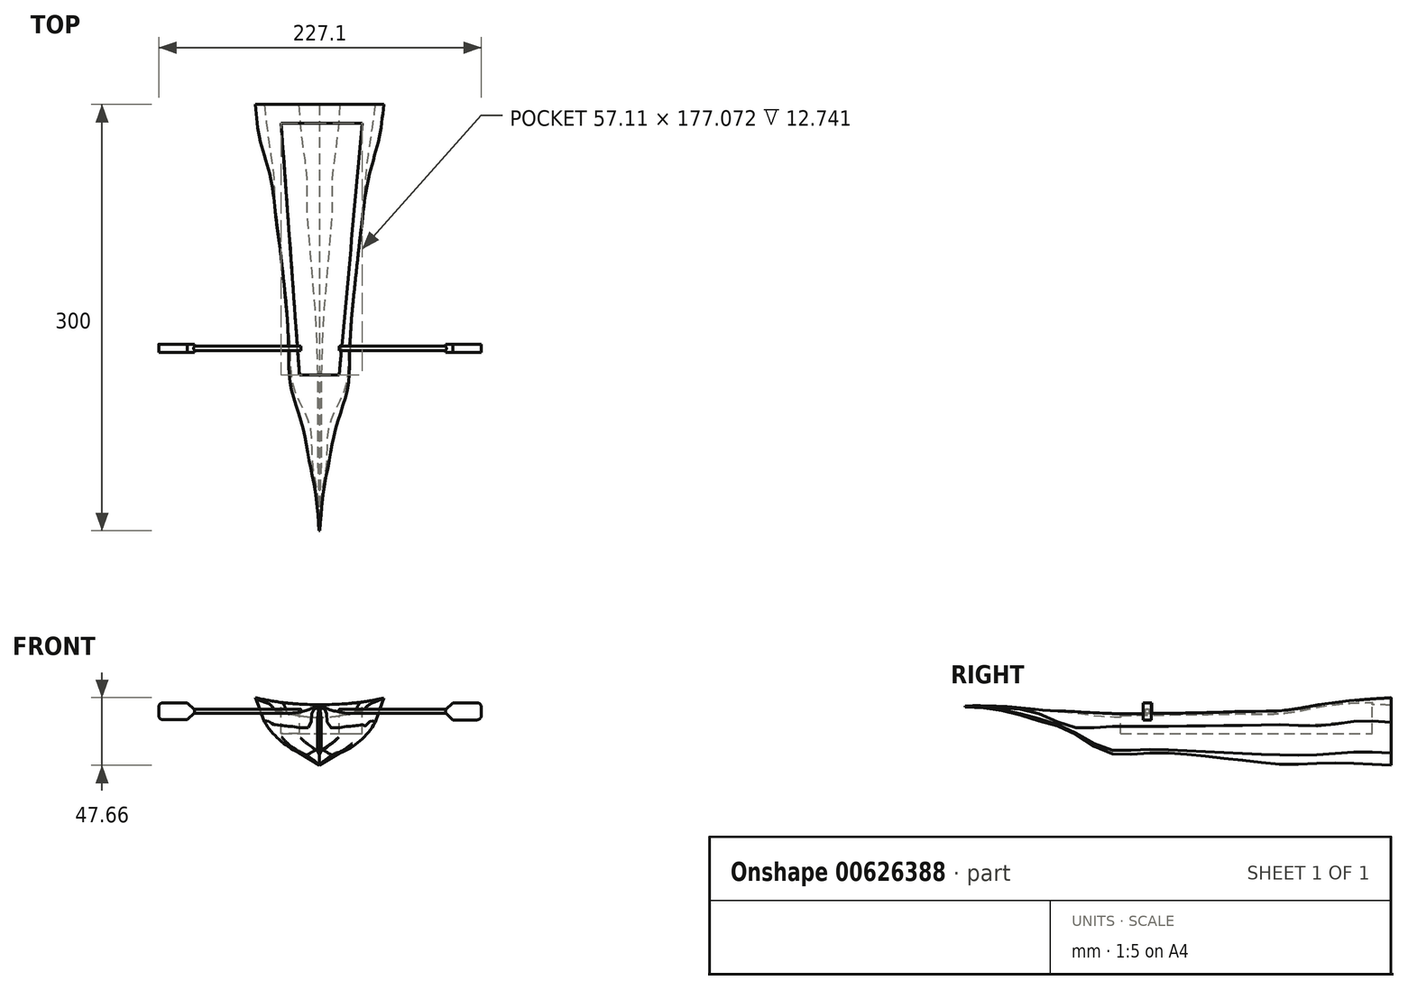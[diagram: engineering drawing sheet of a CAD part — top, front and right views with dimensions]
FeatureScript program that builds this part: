
annotation { "Feature Type Name" : "Feature", "Feature Type Description" : "" }
export const myFeature = defineFeature(function(context is Context, id is Id, definition is map)
    precondition{}
    {
        {
            var Q0;
            Q0=qCreatedBy(makeId("Front.planeOp"),FACE);
            var sketch = newSketch(context, id + "F0", { "sketchPlane" : qUnion([Q0])});
            skLineSegment(sketch, "E0", {"start": v(0, 0) * mm, "end": v(-7, 5) * mm});
            skLineSegment(sketch, "E1", {"start": v(7, 5) * mm, "end": v(0, 0) * mm});
            skArc(sketch, "E2", {"start": v(-27.91, 34.76) * mm, "mid": v(0, 30.75) * mm, "end": v(27.91, 34.76) * mm});
            skArc(sketch, "E3", {"start": v(-27.91, 25) * mm, "mid": v(-19.33, 13.04) * mm, "end": v(-7, 5) * mm});
            skArc(sketch, "E4", {"start": v(7, 5) * mm, "mid": v(19.33, 13.04) * mm, "end": v(27.91, 25) * mm});
            skPoint(sketch, "E5.start.orphan", {"position": v(7, 25) * mm});
            skPoint(sketch, "E6.end.orphan", {"position": v(27.91, 5) * mm});
            skPoint(sketch, "E7.end.orphan", {"position": v(-7, 25) * mm});
            skLineSegment(sketch, "E8", {"start": v(27.91, 25) * mm, "end": v(27.91, 34.76) * mm});
            skLineSegment(sketch, "E9", {"start": v(-27.91, 25) * mm, "end": v(-27.91, 34.76) * mm});
            skPoint(sketch, "E10.orphan", {"position": v(-27.91, 35) * mm});
            skPoint(sketch, "E11.orphan", {"position": v(27.91, 35) * mm});
            skSolve(sketch);
        }
        {
            var Q0;
            Q0=makeQuery(id+"F0.imprint","IMPRINT",FACE,{"disambiguationData":[TD([[makeQuery(id+"F0.imprint","IMPRINT",EDGE,{"derivedFrom":sQuery(id+"F0.wireOp",EDGE,"E0")}),-1.0]])]});
            cPlane(context, id + "F1", {"entities" : qUnion([Q0]), "cplaneType" : CPlaneType.OFFSET, "offset" : 25 * mm, "width" : 150 * mm, "height" : 150 * mm});
        }
        {
            var Q0;
            Q0=qCreatedBy(id+"F1.planeOp",FACE);
            var sketch = newSketch(context, id + "F2", { "sketchPlane" : qUnion([Q0])});
            skLineSegment(sketch, "E12", {"start": v(0, 0) * mm, "end": v(0, 2.5) * mm});
            skLineSegment(sketch, "E13", {"start": v(0, 2.5) * mm, "end": v(4.92, 6.19) * mm});
            skArc(sketch, "E14", {"start": v(4.92, 6.19) * mm, "mid": v(16.37, 14.01) * mm, "end": v(25.2, 24.7) * mm});
            skLineSegment(sketch, "E15", {"start": v(0, 2.5) * mm, "end": v(0, 5.33) * mm});
            skLineSegment(sketch, "E16", {"start": v(0, 2.5) * mm, "end": v(-4.92, 6.19) * mm});
            skArc(sketch, "E17", {"start": v(-25.01, 24.7) * mm, "mid": v(-16.4, 13.89) * mm, "end": v(-4.92, 6.19) * mm});
            skPoint(sketch, "E18.end.orphan", {"position": v(-25.01, 31.8) * mm});
            skLineSegment(sketch, "E19", {"start": v(-25.01, 24.7) * mm, "end": v(-25.01, 34.04) * mm});
            skPoint(sketch, "E20.end.orphan", {"position": v(25.2, 31.8) * mm});
            skLineSegment(sketch, "E21", {"start": v(25.2, 24.7) * mm, "end": v(25.2, 34.03) * mm});
            skArc(sketch, "E22", {"start": v(-25.01, 34.04) * mm, "mid": v(0.1, 30.82) * mm, "end": v(25.2, 34.03) * mm});
            skSolve(sketch);
        }
        {
            var Q0;
            Q0=makeQuery(id+"F2.imprint","IMPRINT",FACE,{"disambiguationData":[TD([[makeQuery(id+"F2.imprint","IMPRINT",EDGE,{"derivedFrom":sQuery(id+"F2.wireOp",EDGE,"E13")}),1.0]])]});
            cPlane(context, id + "F3", {"entities" : qUnion([Q0]), "cplaneType" : CPlaneType.OFFSET, "offset" : 25 * mm, "width" : 150 * mm, "height" : 150 * mm});
        }
        {
            var Q0;
            Q0=qCreatedBy(id+"F3.planeOp",FACE);
            var sketch = newSketch(context, id + "F4", { "sketchPlane" : qUnion([Q0])});
            skLineSegment(sketch, "E23", {"start": v(0, 5.17) * mm, "end": v(2.84, 7.4) * mm});
            skLineSegment(sketch, "E24", {"start": v(0, 5.17) * mm, "end": v(-2.84, 7.4) * mm});
            skArc(sketch, "E25", {"start": v(2.84, 7.4) * mm, "mid": v(14, 14.51) * mm, "end": v(22.71, 24.47) * mm});
            skArc(sketch, "E26", {"start": v(-22.66, 24.44) * mm, "mid": v(-13.98, 14.49) * mm, "end": v(-2.84, 7.4) * mm});
            skLineSegment(sketch, "E27", {"start": v(-22.66, 24.44) * mm, "end": v(-22.66, 33.5) * mm});
            skLineSegment(sketch, "E28", {"start": v(22.71, 24.47) * mm, "end": v(22.71, 33.46) * mm});
            skArc(sketch, "E29", {"start": v(-22.66, 33.5) * mm, "mid": v(0.03, 30.83) * mm, "end": v(22.71, 33.46) * mm});
            skSolve(sketch);
        }
        {
            var Q0;
            Q0=qCreatedBy(id+"F3.planeOp",FACE);
            cPlane(context, id + "F5", {"entities" : qUnion([Q0]), "cplaneType" : CPlaneType.OFFSET, "offset" : 25 * mm, "width" : 150 * mm, "height" : 150 * mm});
        }
        {
            var Q0;
            Q0=qCreatedBy(makeId("Front.planeOp"),FACE);
            cPlane(context, id + "F6", {"entities" : qUnion([Q0]), "cplaneType" : CPlaneType.OFFSET, "offset" : 25 * mm, "oppositeDirection" : true, "width" : 150 * mm, "height" : 150 * mm});
        }
        {
            var Q0;
            Q0=qCreatedBy(id+"F6.planeOp",FACE);
            var sketch = newSketch(context, id + "F7", { "sketchPlane" : qUnion([Q0])});
            skLineSegment(sketch, "E30", {"start": v(-8.83, 3.96) * mm, "end": v(0, -2.66) * mm});
            skLineSegment(sketch, "E31", {"start": v(8.85, 3.96) * mm, "end": v(0, -2.66) * mm});
            skArc(sketch, "E32", {"start": v(-31.1, 25.34) * mm, "mid": v(-22.18, 12.34) * mm, "end": v(-8.83, 3.96) * mm});
            skArc(sketch, "E33", {"start": v(8.85, 3.96) * mm, "mid": v(22.33, 12.1) * mm, "end": v(30.9, 25.3) * mm});
            skLineSegment(sketch, "E34", {"start": v(30.9, 25.3) * mm, "end": v(30.9, 35.5) * mm});
            skLineSegment(sketch, "E35", {"start": v(-31.1, 25.34) * mm, "end": v(-31.1, 35.5) * mm});
            skArc(sketch, "E36", {"start": v(-31.1, 35.5) * mm, "mid": v(-0.1, 30.84) * mm, "end": v(30.9, 35.5) * mm});
            skSolve(sketch);
        }
        {
            var Q0;
            Q0=qCreatedBy(id+"F5.planeOp",FACE);
            var sketch = newSketch(context, id + "F8", { "sketchPlane" : qUnion([Q0])});
            skLineSegment(sketch, "E37", {"start": v(0, 0) * mm, "end": v(0, 5.2) * mm});
            skLineSegment(sketch, "E38", {"start": v(0, 5.2) * mm, "end": v(1.7, 7.89) * mm});
            skLineSegment(sketch, "E39", {"start": v(0, 5.2) * mm, "end": v(0, 15.24) * mm});
            skLineSegment(sketch, "E40", {"start": v(0, 5.2) * mm, "end": v(-1.7, 7.89) * mm});
            skArc(sketch, "E41", {"start": v(-20.62, 24.18) * mm, "mid": v(-12.06, 14.98) * mm, "end": v(-1.7, 7.89) * mm});
            skArc(sketch, "E42", {"start": v(1.7, 7.89) * mm, "mid": v(11.95, 14.95) * mm, "end": v(20.33, 24.16) * mm});
            skLineSegment(sketch, "E43", {"start": v(20.33, 24.16) * mm, "end": v(21.38, 33.19) * mm});
            skLineSegment(sketch, "E44", {"start": v(-20.62, 24.18) * mm, "end": v(-21.68, 33.2) * mm});
            skArc(sketch, "E45", {"start": v(-21.68, 33.2) * mm, "mid": v(-0.15, 30.86) * mm, "end": v(21.38, 33.19) * mm});
            skSolve(sketch);
        }
        {
            var Q0;
            Q0=qCreatedBy(id+"F5.planeOp",FACE);
            cPlane(context, id + "F9", {"entities" : qUnion([Q0]), "cplaneType" : CPlaneType.OFFSET, "offset" : 25 * mm, "width" : 150 * mm, "height" : 150 * mm});
        }
        {
            var Q0;
            Q0=qCreatedBy(id+"F6.planeOp",FACE);
            cPlane(context, id + "F10", {"entities" : qUnion([Q0]), "cplaneType" : CPlaneType.OFFSET, "offset" : 25 * mm, "oppositeDirection" : true, "width" : 150 * mm, "height" : 150 * mm});
        }
        {
            var Q0;
            Q0=qCreatedBy(id+"F10.planeOp",FACE);
            var sketch = newSketch(context, id + "F11", { "sketchPlane" : qUnion([Q0])});
            skLineSegment(sketch, "E46", {"start": v(0, -1.8) * mm, "end": v(-9.14, 4.4) * mm});
            skLineSegment(sketch, "E47", {"start": v(0, -1.8) * mm, "end": v(9.14, 4.4) * mm});
            skArc(sketch, "E48", {"start": v(9.14, 4.4) * mm, "mid": v(22.92, 12.09) * mm, "end": v(32.5, 24.6) * mm});
            skArc(sketch, "E49", {"start": v(-32.38, 25.49) * mm, "mid": v(-22.75, 12.75) * mm, "end": v(-9.14, 4.4) * mm});
            skLineSegment(sketch, "E50", {"start": v(-32.38, 25.49) * mm, "end": v(-34.73, 39.5) * mm});
            skLineSegment(sketch, "E51", {"start": v(32.5, 24.6) * mm, "end": v(35.04, 39.5) * mm});
            skArc(sketch, "E52", {"start": v(-34.73, 39.5) * mm, "mid": v(0.15, 36.4) * mm, "end": v(35.04, 39.5) * mm});
            skSolve(sketch);
        }
        {
            var Q0;
            Q0=qCreatedBy(id+"F10.planeOp",FACE);
            cPlane(context, id + "F12", {"entities" : qUnion([Q0]), "cplaneType" : CPlaneType.OFFSET, "offset" : 25 * mm, "oppositeDirection" : true, "width" : 150 * mm, "height" : 150 * mm});
        }
        {
            var Q0;
            Q0=qCreatedBy(id+"F12.planeOp",FACE);
            var sketch = newSketch(context, id + "F13", { "sketchPlane" : qUnion([Q0])});
            skLineSegment(sketch, "E53", {"start": v(0, -1.91) * mm, "end": v(-12.35, 6.1) * mm});
            skLineSegment(sketch, "E54", {"start": v(0, -1.91) * mm, "end": v(12.35, 6.1) * mm});
            skArc(sketch, "E55", {"start": v(-35.84, 27.87) * mm, "mid": v(-25.75, 15.2) * mm, "end": v(-12.35, 6.1) * mm});
            skLineSegment(sketch, "E56", {"start": v(-35.84, 27.87) * mm, "end": v(-41.84, 42.55) * mm});
            skLineSegment(sketch, "E57", {"start": v(35.75, 27.87) * mm, "end": v(41.75, 42.55) * mm});
            skArc(sketch, "E58", {"start": v(-41.84, 42.55) * mm, "mid": v(-0.05, 39.36) * mm, "end": v(41.75, 42.55) * mm});
            skArc(sketch, "E59", {"start": v(12.35, 6.1) * mm, "mid": v(26.45, 14.4) * mm, "end": v(35.75, 27.87) * mm});
            skSolve(sketch);
        }
        {
            var Q0;
            Q0=qCreatedBy(id+"F12.planeOp",FACE);
            cPlane(context, id + "F14", {"entities" : qUnion([Q0]), "cplaneType" : CPlaneType.OFFSET, "offset" : 25 * mm, "oppositeDirection" : true, "width" : 150 * mm, "height" : 150 * mm});
        }
        {
            var Q0;
            Q0=qCreatedBy(id+"F14.planeOp",FACE);
            var sketch = newSketch(context, id + "F15", { "sketchPlane" : qUnion([Q0])});
            skLineSegment(sketch, "E60", {"start": v(0, -3.25) * mm, "end": v(-14.6, 5.86) * mm});
            skLineSegment(sketch, "E61", {"start": v(0, -3.25) * mm, "end": v(0, -1.07) * mm});
            skArc(sketch, "E62", {"start": v(-38.72, 27.45) * mm, "mid": v(-28.26, 14.88) * mm, "end": v(-14.6, 5.86) * mm});
            skPoint(sketch, "E63.end.orphan", {"position": v(14.6, 5.86) * mm});
            skLineSegment(sketch, "E64", {"start": v(0, -3.25) * mm, "end": v(14.32, 5.33) * mm});
            skArc(sketch, "E65", {"start": v(14.32, 5.33) * mm, "mid": v(28.68, 14.05) * mm, "end": v(39.32, 27.05) * mm});
            skLineSegment(sketch, "E66", {"start": v(39.32, 27.05) * mm, "end": v(45.35, 44.15) * mm});
            skLineSegment(sketch, "E67", {"start": v(-38.72, 27.45) * mm, "end": v(-44.96, 44.4) * mm});
            skArc(sketch, "E68", {"start": v(-44.96, 44.4) * mm, "mid": v(0.18, 39.17) * mm, "end": v(45.35, 44.15) * mm});
            skSolve(sketch);
        }
        {
            var Q0;
            Q0=qCreatedBy(id+"F9.planeOp",FACE);
            var sketch = newSketch(context, id + "F16", { "sketchPlane" : qUnion([Q0])});
            skLineSegment(sketch, "E69", {"start": v(0, 6) * mm, "end": v(1.23, 8.16) * mm});
            skLineSegment(sketch, "E70", {"start": v(0, 6) * mm, "end": v(-1.24, 8.16) * mm});
            skArc(sketch, "E71", {"start": v(1.23, 8.16) * mm, "mid": v(10.4, 15.25) * mm, "end": v(17.92, 24.05) * mm});
            skArc(sketch, "E72", {"start": v(-18.07, 23.97) * mm, "mid": v(-10.38, 15.3) * mm, "end": v(-1.24, 8.16) * mm});
            skLineSegment(sketch, "E73", {"start": v(-18.07, 23.97) * mm, "end": v(-19.75, 33.38) * mm});
            skLineSegment(sketch, "E74", {"start": v(17.92, 24.05) * mm, "end": v(19.83, 33.3) * mm});
            skArc(sketch, "E75", {"start": v(-19.75, 33.38) * mm, "mid": v(0.03, 30.84) * mm, "end": v(19.83, 33.3) * mm});
            skSolve(sketch);
        }
        {
            var Q0;
            Q0=qCreatedBy(id+"F9.planeOp",FACE);
            cPlane(context, id + "F17", {"entities" : qUnion([Q0]), "cplaneType" : CPlaneType.OFFSET, "offset" : 25 * mm, "width" : 150 * mm, "height" : 150 * mm});
        }
        {
            var Q0;
            Q0=qCreatedBy(id+"F17.planeOp",FACE);
            var sketch = newSketch(context, id + "F18", { "sketchPlane" : qUnion([Q0])});
            skPoint(sketch, "E76.top.end.orphan", {"position": v(-12.21, 6.12) * mm});
            skPoint(sketch, "E76.left.end.orphan", {"position": v(12.21, 6.12) * mm});
            skPoint(sketch, "E77", {"position": v(0, 36.5) * mm});
            skPoint(sketch, "E78", {"position": v(-12.36, 34.65) * mm});
            skArc(sketch, "E79", {"start": v(-12.36, 34.65) * mm, "mid": v(0, 33.63) * mm, "end": v(12.36, 34.65) * mm});
            skPoint(sketch, "E80.top.start.orphan", {"position": v(-12.36, 38.34) * mm});
            skPoint(sketch, "E80.right.end.orphan", {"position": v(12.36, 38.34) * mm});
            skPoint(sketch, "E81.middle", {"position": v(0, 26.55) * mm});
            skArc(sketch, "E82", {"start": v(7.07, 23.72) * mm, "mid": v(10.26, 28.92) * mm, "end": v(12.36, 34.65) * mm});
            skArc(sketch, "E83", {"start": v(-12.36, 34.65) * mm, "mid": v(-10.3, 28.9) * mm, "end": v(-7.07, 23.72) * mm});
            skPoint(sketch, "E83.endSnap0", {"position": v(-7.07, 26.55) * mm});
            skPoint(sketch, "E84.orphan", {"position": v(-7.07, 33.96) * mm});
            skPoint(sketch, "E85.orphan", {"position": v(7.07, 33.96) * mm});
            skPoint(sketch, "E81.top.end.orphan", {"position": v(-7.07, 19.14) * mm});
            skPoint(sketch, "E81.top.start.orphan", {"position": v(7.07, 19.14) * mm});
            skPoint(sketch, "E86.start.orphan", {"position": v(0, 20.2) * mm});
            skLineSegment(sketch, "E87", {"start": v(-7.07, 23.72) * mm, "end": v(-1.16, 21.26) * mm});
            skLineSegment(sketch, "E88", {"start": v(-1.16, 21.26) * mm, "end": v(0, 20.2) * mm});
            skLineSegment(sketch, "E89", {"start": v(0, 20.2) * mm, "end": v(1.16, 21.26) * mm});
            skLineSegment(sketch, "E90", {"start": v(7.07, 23.72) * mm, "end": v(1.16, 21.26) * mm});
            skPoint(sketch, "E91.top.end.orphan", {"position": v(1.16, 19.13) * mm});
            skPoint(sketch, "E91.left.end.orphan", {"position": v(-1.16, 19.13) * mm});
            skSolve(sketch);
        }
        {
            var Q0;
            Q0=qCreatedBy(id+"F17.planeOp",FACE);
            cPlane(context, id + "F19", {"entities" : qUnion([Q0]), "cplaneType" : CPlaneType.OFFSET, "offset" : 25 * mm, "width" : 150 * mm, "height" : 150 * mm});
        }
        {
            var Q0;
            Q0=qCreatedBy(id+"F19.planeOp",FACE);
            var sketch = newSketch(context, id + "F20", { "sketchPlane" : qUnion([Q0])});
            skPoint(sketch, "E92", {"position": v(0, 28.74) * mm});
            skLineSegment(sketch, "E93", {"start": v(0, 28.74) * mm, "end": v(1.2, 30.13) * mm});
            skLineSegment(sketch, "E94", {"start": v(0, 28.74) * mm, "end": v(-1.2, 30.13) * mm});
            skPoint(sketch, "E95.top.start.orphan", {"position": v(1.2, 27.36) * mm});
            skPoint(sketch, "E95.right.end.orphan", {"position": v(-1.2, 27.36) * mm});
            skPoint(sketch, "E96.top.end.orphan", {"position": v(-4.76, 21.83) * mm});
            skPoint(sketch, "E96.top.start.orphan", {"position": v(4.76, 21.83) * mm});
            skPoint(sketch, "E97.top.end.orphan", {"position": v(-12.6, 14.32) * mm});
            skPoint(sketch, "E97.top.start.orphan", {"position": v(12.6, 14.32) * mm});
            skPoint(sketch, "E98.start.orphan", {"position": v(-12.6, 43.17) * mm});
            skPoint(sketch, "E99.end.orphan", {"position": v(12.6, 43.17) * mm});
            skPoint(sketch, "E100.end.orphan", {"position": v(4.76, 35.66) * mm});
            skPoint(sketch, "E101.end.orphan", {"position": v(-4.76, 35.66) * mm});
            skPoint(sketch, "E102.top.end.orphan", {"position": v(-4.37, 23.59) * mm});
            skPoint(sketch, "E102.top.start.orphan", {"position": v(4.37, 23.59) * mm});
            skLineSegment(sketch, "E103", {"start": v(1.2, 30.13) * mm, "end": v(5.1, 33.9) * mm});
            skLineSegment(sketch, "E104", {"start": v(-1.2, 30.13) * mm, "end": v(-5.36, 33.9) * mm});
            skPoint(sketch, "E105.orphan", {"position": v(-4.37, 33.9) * mm});
            skPoint(sketch, "E106.end.orphan", {"position": v(4.37, 33.9) * mm});
            skPoint(sketch, "E107.top.end.orphan", {"position": v(-6.68, 20.51) * mm});
            skPoint(sketch, "E107.top.start.orphan", {"position": v(6.68, 20.51) * mm});
            skPoint(sketch, "E107.bottom.end.orphan", {"position": v(-6.68, 36.97) * mm});
            skPoint(sketch, "E107.bottom.start.orphan", {"position": v(6.68, 36.97) * mm});
            skArc(sketch, "E108", {"start": v(5.1, 33.9) * mm, "mid": v(6.22, 34.84) * mm, "end": v(7.01, 36.08) * mm});
            skArc(sketch, "E109", {"start": v(-7.23, 36.08) * mm, "mid": v(-6.47, 34.84) * mm, "end": v(-5.36, 33.9) * mm});
            skArc(sketch, "E110", {"start": v(-7.23, 36.08) * mm, "mid": v(-0.1, 35.56) * mm, "end": v(7.01, 36.08) * mm});
            skSolve(sketch);
        }
        {
            var Q0;
            Q0=qCreatedBy(id+"F19.planeOp",FACE);
            cPlane(context, id + "F21", {"entities" : qUnion([Q0]), "cplaneType" : CPlaneType.OFFSET, "offset" : 25 * mm, "width" : 150 * mm, "height" : 150 * mm});
        }
        {
            var Q0;
            Q0=qCreatedBy(id+"F21.planeOp",FACE);
            var sketch = newSketch(context, id + "F22", { "sketchPlane" : qUnion([Q0])});
            skPoint(sketch, "E111", {"position": v(0, 35.66) * mm});
            skLineSegment(sketch, "E112", {"start": v(0, 35.66) * mm, "end": v(0.41, 36.23) * mm});
            skLineSegment(sketch, "E113", {"start": v(1.33, 37.34) * mm, "end": v(0.41, 36.23) * mm});
            skLineSegment(sketch, "E114", {"start": v(-0.41, 36.23) * mm, "end": v(-1.33, 37.34) * mm});
            skLineSegment(sketch, "E115", {"start": v(0, 35.66) * mm, "end": v(-0.41, 36.23) * mm});
            skArc(sketch, "E116", {"start": v(1.33, 37.34) * mm, "mid": v(1.96, 37.77) * mm, "end": v(2.52, 38.3) * mm});
            skArc(sketch, "E117", {"start": v(-2.52, 38.3) * mm, "mid": v(-1.96, 37.78) * mm, "end": v(-1.33, 37.34) * mm});
            skPoint(sketch, "E118.top.end.orphan", {"position": v(-1.33, 33.99) * mm});
            skPoint(sketch, "E118.top.start.orphan", {"position": v(1.33, 33.99) * mm});
            skPoint(sketch, "E119.top.end.orphan", {"position": v(-2.52, 33.02) * mm});
            skPoint(sketch, "E119.left.end.orphan", {"position": v(2.52, 33.02) * mm});
            skPoint(sketch, "E120.top.start.orphan", {"position": v(0.41, 35.1) * mm});
            skPoint(sketch, "E120.right.end.orphan", {"position": v(-0.41, 35.1) * mm});
            skArc(sketch, "E121", {"start": v(-2.52, 38.3) * mm, "mid": v(0, 38.12) * mm, "end": v(2.52, 38.3) * mm});
            skSolve(sketch);
        }
        {
            var Q0;
            Q0=qCreatedBy(id+"F21.planeOp",FACE);
            cPlane(context, id + "F23", {"entities" : qUnion([Q0]), "cplaneType" : CPlaneType.OFFSET, "offset" : 25 * mm, "width" : 150 * mm, "height" : 150 * mm});
        }
        {
            var Q0;
            Q0=qCreatedBy(id+"F23.planeOp",FACE);
            var sketch = newSketch(context, id + "F24", { "sketchPlane" : qUnion([Q0])});
            skArc(sketch, "E122", {"start": v(-0.4, 38.6) * mm, "mid": v(0, 38.53) * mm, "end": v(0.4, 38.6) * mm});
            skArc(sketch, "E123", {"start": v(0.25, 38.29) * mm, "mid": v(0.35, 38.43) * mm, "end": v(0.4, 38.6) * mm});
            skArc(sketch, "E124", {"start": v(-0.4, 38.6) * mm, "mid": v(-0.35, 38.43) * mm, "end": v(-0.25, 38.29) * mm});
            skLineSegment(sketch, "E125", {"start": v(0.05, 38.08) * mm, "end": v(0.25, 38.29) * mm});
            skLineSegment(sketch, "E126", {"start": v(-0.05, 38.08) * mm, "end": v(-0.25, 38.29) * mm});
            skLineSegment(sketch, "E127", {"start": v(-0.05, 38.08) * mm, "end": v(0, 38) * mm});
            skLineSegment(sketch, "E128", {"start": v(0, 38) * mm, "end": v(0.05, 38.08) * mm});
            skSolve(sketch);
        }
        {
            var Q0;
            Q0=makeQuery(id+"F15.imprint","IMPRINT",FACE,{"disambiguationData":[TD([[makeQuery(id+"F15.imprint","IMPRINT",EDGE,{"derivedFrom":sQuery(id+"F15.wireOp",EDGE,"E60")}),-1.0]])]});
            var Q1;
            Q1=makeQuery(id+"F13.imprint","IMPRINT",FACE,{"disambiguationData":[TD([[makeQuery(id+"F13.imprint","IMPRINT",EDGE,{"derivedFrom":sQuery(id+"F13.wireOp",EDGE,"E53")}),-1.0]])]});
            var Q2;
            Q2=makeQuery(id+"F11.imprint","IMPRINT",FACE,{"disambiguationData":[TD([[makeQuery(id+"F11.imprint","IMPRINT",EDGE,{"derivedFrom":sQuery(id+"F11.wireOp",EDGE,"E46")}),-1.0]])]});
            var Q3;
            Q3=makeQuery(id+"F7.imprint","IMPRINT",FACE,{"disambiguationData":[TD([[makeQuery(id+"F7.imprint","IMPRINT",EDGE,{"derivedFrom":sQuery(id+"F7.wireOp",EDGE,"E30")}),1.0]])]});
            var Q4;
            Q4=makeQuery(id+"F0.imprint","IMPRINT",FACE,{"disambiguationData":[TD([[makeQuery(id+"F0.imprint","IMPRINT",EDGE,{"derivedFrom":sQuery(id+"F0.wireOp",EDGE,"E0")}),-1.0]])]});
            var Q5;
            Q5=makeQuery(id+"F2.imprint","IMPRINT",FACE,{"disambiguationData":[TD([[makeQuery(id+"F2.imprint","IMPRINT",EDGE,{"derivedFrom":sQuery(id+"F2.wireOp",EDGE,"E13")}),1.0]])]});
            var Q6;
            Q6=makeQuery(id+"F4.imprint","IMPRINT",FACE,{"disambiguationData":[TD([[makeQuery(id+"F4.imprint","IMPRINT",EDGE,{"derivedFrom":sQuery(id+"F4.wireOp",EDGE,"E23")}),1.0]])]});
            var Q7;
            Q7=makeQuery(id+"F8.imprint","IMPRINT",FACE,{"disambiguationData":[TD([[makeQuery(id+"F8.imprint","IMPRINT",EDGE,{"derivedFrom":sQuery(id+"F8.wireOp",EDGE,"E38")}),1.0]])]});
            var Q8;
            Q8=makeQuery(id+"F16.imprint","IMPRINT",FACE,{"disambiguationData":[TD([[makeQuery(id+"F16.imprint","IMPRINT",EDGE,{"derivedFrom":sQuery(id+"F16.wireOp",EDGE,"E69")}),1.0]])]});
            var Q9;
            Q9=makeQuery(id+"F18.imprint","IMPRINT",FACE,{"disambiguationData":[TD([[makeQuery(id+"F18.imprint","IMPRINT",EDGE,{"derivedFrom":sQuery(id+"F18.wireOp",EDGE,"E79")}),-1.0]])]});
            var Q10;
            Q10=makeQuery(id+"F20.imprint","IMPRINT",FACE,{"disambiguationData":[TD([[makeQuery(id+"F20.imprint","IMPRINT",EDGE,{"derivedFrom":sQuery(id+"F20.wireOp",EDGE,"E93")}),1.0]])]});
            var Q11;
            Q11=makeQuery(id+"F22.imprint","IMPRINT",FACE,{"disambiguationData":[TD([[makeQuery(id+"F22.imprint","IMPRINT",EDGE,{"derivedFrom":sQuery(id+"F22.wireOp",EDGE,"E112")}),1.0]])]});
            var Q12;
            Q12=makeQuery(id+"F24.imprint","IMPRINT",FACE,{"disambiguationData":[TD([[makeQuery(id+"F24.imprint","IMPRINT",EDGE,{"derivedFrom":sQuery(id+"F24.wireOp",EDGE,"E122")}),-1.0]])]});
            var Q13;
            Q13=makeQuery(id+"F15.imprint","IMPRINT",FACE,{"disambiguationData":[TD([[makeQuery(id+"F15.imprint","IMPRINT",EDGE,{"derivedFrom":sQuery(id+"F15.wireOp",EDGE,"E60")}),-1.0]])]});
            var Q14;
            Q14=makeQuery(id+"F13.imprint","IMPRINT",FACE,{"disambiguationData":[TD([[makeQuery(id+"F13.imprint","IMPRINT",EDGE,{"derivedFrom":sQuery(id+"F13.wireOp",EDGE,"E53")}),-1.0]])]});
            var Q15;
            Q15=makeQuery(id+"F11.imprint","IMPRINT",FACE,{"disambiguationData":[TD([[makeQuery(id+"F11.imprint","IMPRINT",EDGE,{"derivedFrom":sQuery(id+"F11.wireOp",EDGE,"E46")}),-1.0]])]});
            var Q16;
            Q16=makeQuery(id+"F7.imprint","IMPRINT",FACE,{"disambiguationData":[TD([[makeQuery(id+"F7.imprint","IMPRINT",EDGE,{"derivedFrom":sQuery(id+"F7.wireOp",EDGE,"E30")}),1.0]])]});
            var Q17;
            Q17=makeQuery(id+"F0.imprint","IMPRINT",FACE,{"disambiguationData":[TD([[makeQuery(id+"F0.imprint","IMPRINT",EDGE,{"derivedFrom":sQuery(id+"F0.wireOp",EDGE,"E0")}),-1.0]])]});
            var Q18;
            Q18=makeQuery(id+"F2.imprint","IMPRINT",FACE,{"disambiguationData":[TD([[makeQuery(id+"F2.imprint","IMPRINT",EDGE,{"derivedFrom":sQuery(id+"F2.wireOp",EDGE,"E13")}),1.0]])]});
            var Q19;
            Q19=makeQuery(id+"F4.imprint","IMPRINT",FACE,{"disambiguationData":[TD([[makeQuery(id+"F4.imprint","IMPRINT",EDGE,{"derivedFrom":sQuery(id+"F4.wireOp",EDGE,"E23")}),1.0]])]});
            var Q20;
            Q20=makeQuery(id+"F8.imprint","IMPRINT",FACE,{"disambiguationData":[TD([[makeQuery(id+"F8.imprint","IMPRINT",EDGE,{"derivedFrom":sQuery(id+"F8.wireOp",EDGE,"E38")}),1.0]])]});
            var Q21;
            Q21=makeQuery(id+"F16.imprint","IMPRINT",FACE,{"disambiguationData":[TD([[makeQuery(id+"F16.imprint","IMPRINT",EDGE,{"derivedFrom":sQuery(id+"F16.wireOp",EDGE,"E69")}),1.0]])]});
            var Q22;
            Q22=makeQuery(id+"F18.imprint","IMPRINT",FACE,{"disambiguationData":[TD([[makeQuery(id+"F18.imprint","IMPRINT",EDGE,{"derivedFrom":sQuery(id+"F18.wireOp",EDGE,"E79")}),-1.0]])]});
            var Q23;
            Q23=makeQuery(id+"F20.imprint","IMPRINT",FACE,{"disambiguationData":[TD([[makeQuery(id+"F20.imprint","IMPRINT",EDGE,{"derivedFrom":sQuery(id+"F20.wireOp",EDGE,"E93")}),1.0]])]});
            var Q24;
            Q24=makeQuery(id+"F22.imprint","IMPRINT",FACE,{"disambiguationData":[TD([[makeQuery(id+"F22.imprint","IMPRINT",EDGE,{"derivedFrom":sQuery(id+"F22.wireOp",EDGE,"E112")}),1.0]])]});
            var Q25;
            Q25=makeQuery(id+"F24.imprint","IMPRINT",FACE,{"disambiguationData":[TD([[makeQuery(id+"F24.imprint","IMPRINT",EDGE,{"derivedFrom":sQuery(id+"F24.wireOp",EDGE,"E122")}),-1.0]])]});
            loft(context, id + "F25", {"sheetProfilesArray" : [{ "sheetProfileEntities" : qUnion([Q0]) }, { "sheetProfileEntities" : qUnion([Q1]) }, { "sheetProfileEntities" : qUnion([Q2]) }, { "sheetProfileEntities" : qUnion([Q3]) }, { "sheetProfileEntities" : qUnion([Q4]) }, { "sheetProfileEntities" : qUnion([Q5]) }, { "sheetProfileEntities" : qUnion([Q6]) }, { "sheetProfileEntities" : qUnion([Q7]) }, { "sheetProfileEntities" : qUnion([Q8]) }, { "sheetProfileEntities" : qUnion([Q9]) }, { "sheetProfileEntities" : qUnion([Q10]) }, { "sheetProfileEntities" : qUnion([Q11]) }, { "sheetProfileEntities" : qUnion([Q12]) }], "wireProfilesArray" : [{ "wireProfileEntities" : qUnion([Q13]) }, { "wireProfileEntities" : qUnion([Q14]) }, { "wireProfileEntities" : qUnion([Q15]) }, { "wireProfileEntities" : qUnion([Q16]) }, { "wireProfileEntities" : qUnion([Q17]) }, { "wireProfileEntities" : qUnion([Q18]) }, { "wireProfileEntities" : qUnion([Q19]) }, { "wireProfileEntities" : qUnion([Q20]) }, { "wireProfileEntities" : qUnion([Q21]) }, { "wireProfileEntities" : qUnion([Q22]) }, { "wireProfileEntities" : qUnion([Q23]) }, { "wireProfileEntities" : qUnion([Q24]) }, { "wireProfileEntities" : qUnion([Q25]) }]});
        }
        {
            var Q0;
            Q0=qCreatedBy(makeId("Top.planeOp"),FACE);
            cPlane(context, id + "F26", {"entities" : qUnion([Q0]), "cplaneType" : CPlaneType.OFFSET, "offset" : 46 * mm, "width" : 150 * mm, "height" : 150 * mm});
        }
        {
            var Q0;
            Q0=qCreatedBy(id+"F26.planeOp",FACE);
            var sketch = newSketch(context, id + "F27", { "sketchPlane" : qUnion([Q0])});
            skLineSegment(sketch, "E129", {"start": v(-14.07, -90.3) * mm, "end": v(13.94, -90.3) * mm});
            skLineSegment(sketch, "E130", {"start": v(13.94, -90.3) * mm, "end": v(30.22, 86.76) * mm});
            skLineSegment(sketch, "E131", {"start": v(-14.07, -90.3) * mm, "end": v(-26.89, 86.76) * mm});
            skLineSegment(sketch, "E132", {"start": v(-26.89, 86.76) * mm, "end": v(30.22, 86.76) * mm});
            skSolve(sketch);
        }
        {
            var Q0;
            Q0=makeQuery(id+"F27.imprint","IMPRINT",FACE,{"disambiguationData":[TD([[makeQuery(id+"F27.imprint","IMPRINT",EDGE,{"derivedFrom":sQuery(id+"F27.wireOp",EDGE,"E129")}),1.0]])]});
            extrude(context, id + "F28", {"entities" : qUnion([Q0]), "operationType" : NewBodyOperationType.REMOVE, "oppositeDirection" : true, "depth" : 27 * mm, "offsetDistance" : 25 * mm});
        }
        {
            var Q0;
            Q0=qCreatedBy(makeId("Right.planeOp"),FACE);
            cPlane(context, id + "F29", {"entities" : qUnion([Q0]), "cplaneType" : CPlaneType.OFFSET, "offset" : 13.1 * mm, "oppositeDirection" : true, "width" : 150 * mm, "height" : 150 * mm});
        }
        {
            var Q0;
            Q0=qCreatedBy(id+"F29.planeOp",FACE);
            var sketch = newSketch(context, id + "F30", { "sketchPlane" : qUnion([Q0])});
            skCircle(sketch, "E133", {"center": v(-71.65, 34.86) * mm, "radius": 1.5 * mm});
            skSolve(sketch);
        }
        {
            var Q0;
            Q0=makeQuery(id+"F30.imprint","IMPRINT",FACE,{"disambiguationData":[TD([[makeQuery(id+"F30.imprint","IMPRINT",EDGE,{"derivedFrom":sQuery(id+"F30.wireOp",EDGE,"E133")}),1.0]])]});
            extrude(context, id + "F31", {"entities" : qUnion([Q0]), "oppositeDirection" : true, "depth" : 75 * mm, "offsetDistance" : 25 * mm});
        }
        {
            var Q0;
            Q0=makeQuery(id+"F31.opExtrude","CAP_FACE",FACE,{"disambiguationData":[OSD([sQuery(id+"F30.wireOp",EDGE,"E133")])],"isStart":false});
            var sketch = newSketch(context, id + "F32", { "sketchPlane" : qUnion([Q0])});
            skLineSegment(sketch, "E134.bottom", {"start": v(74.65, 28.86) * mm, "end": v(68.65, 28.86) * mm});
            skLineSegment(sketch, "E134.top", {"start": v(74.65, 40.86) * mm, "end": v(68.65, 40.86) * mm});
            skLineSegment(sketch, "E134.left", {"start": v(74.65, 28.86) * mm, "end": v(74.65, 40.86) * mm});
            skLineSegment(sketch, "E134.right", {"start": v(68.65, 28.86) * mm, "end": v(68.65, 40.86) * mm});
            skPoint(sketch, "E134.middle", {"position": v(71.65, 34.86) * mm});
            skSolve(sketch);
        }
        {
            var Q0;
            Q0=makeQuery(id+"F32.imprint","IMPRINT",FACE,{"disambiguationData":[TD([[makeQuery(id+"F32.imprint","IMPRINT",EDGE,{"derivedFrom":makeQuery(id+"F31.opExtrude","CAP_EDGE",EDGE,{"disambiguationData":[OSD([sQuery(id+"F30.wireOp",EDGE,"E133")])],"isStart":false})}),-1.0]])]});
            var Q1;
            Q1=makeQuery(id+"F32.imprint","IMPRINT",FACE,{"disambiguationData":[TD([[makeQuery(id+"F32.imprint","IMPRINT",EDGE,{"derivedFrom":sQuery(id+"F32.wireOp",EDGE,"E134.bottom")}),-1.0]])]});
            extrude(context, id + "F33", {"entities" : qUnion([Q0, Q1]), "operationType" : NewBodyOperationType.ADD, "depth" : 25 * mm, "offsetDistance" : 25 * mm});
        }
        {
            var Q0;
            Q0=makeQuery(id+"F33.opExtrude","CAP_EDGE",EDGE,{"disambiguationData":[OSD([sQuery(id+"F32.wireOp",EDGE,"E134.top")])],"isStart":true});
            var Q1;
            Q1=makeQuery(id+"F33.opExtrude","CAP_EDGE",EDGE,{"disambiguationData":[OSD([sQuery(id+"F32.wireOp",EDGE,"E134.bottom")])],"isStart":true});
            chamfer(context, id + "F34", {"entities" : qUnion([Q0, Q1]), "width" : 5 * mm, "tangentPropagation" : true});
        }
        {
            var Q0;
            Q0=makeQuery(id+"F33.opExtrude","CAP_EDGE",EDGE,{"disambiguationData":[OSD([sQuery(id+"F32.wireOp",EDGE,"E134.top")])],"isStart":false});
            var Q1;
            Q1=makeQuery(id+"F33.opExtrude","CAP_EDGE",EDGE,{"disambiguationData":[OSD([sQuery(id+"F32.wireOp",EDGE,"E134.bottom")])],"isStart":false});
            fillet(context, id + "F35", {"entities" : qUnion([Q0, Q1]), "radius" : 3 * mm, "tangentPropagation" : true, "allowEdgeOverflow" : false});
        }
        {
            var Q0;
            Q0=qCreatedBy(makeId("Right.planeOp"),FACE);
            cPlane(context, id + "F36", {"entities" : qUnion([Q0]), "cplaneType" : CPlaneType.OFFSET, "offset" : 14 * mm, "width" : 150 * mm, "height" : 150 * mm});
        }
        {
            var Q0;
            Q0=qCreatedBy(id+"F36.planeOp",FACE);
            var sketch = newSketch(context, id + "F37", { "sketchPlane" : qUnion([Q0])});
            skCircle(sketch, "E135", {"center": v(-71.66, 34.8) * mm, "radius": 1.5 * mm});
            skSolve(sketch);
        }
        {
            var Q0;
            Q0=makeQuery(id+"F37.imprint","IMPRINT",FACE,{"disambiguationData":[TD([[makeQuery(id+"F37.imprint","IMPRINT",EDGE,{"derivedFrom":sQuery(id+"F37.wireOp",EDGE,"E135")}),1.0]])]});
            extrude(context, id + "F38", {"entities" : qUnion([Q0]), "depth" : 75 * mm, "offsetDistance" : 25 * mm});
        }
        {
            var Q0;
            Q0=makeQuery(id+"F38.opExtrude","CAP_FACE",FACE,{"disambiguationData":[OSD([sQuery(id+"F37.wireOp",EDGE,"E135")])],"isStart":false});
            var sketch = newSketch(context, id + "F39", { "sketchPlane" : qUnion([Q0])});
            skLineSegment(sketch, "E136.bottom", {"start": v(-68.66, 28.8) * mm, "end": v(-74.66, 28.8) * mm});
            skLineSegment(sketch, "E136.top", {"start": v(-68.66, 40.8) * mm, "end": v(-74.66, 40.8) * mm});
            skLineSegment(sketch, "E136.left", {"start": v(-68.66, 28.8) * mm, "end": v(-68.66, 40.8) * mm});
            skLineSegment(sketch, "E136.right", {"start": v(-74.66, 28.8) * mm, "end": v(-74.66, 40.8) * mm});
            skPoint(sketch, "E136.middle", {"position": v(-71.66, 34.8) * mm});
            skSolve(sketch);
        }
        {
            var Q0;
            Q0=makeQuery(id+"F39.imprint","IMPRINT",FACE,{"disambiguationData":[TD([[makeQuery(id+"F39.imprint","IMPRINT",EDGE,{"derivedFrom":sQuery(id+"F39.wireOp",EDGE,"E136.bottom")}),-1.0]])]});
            var Q1;
            Q1=makeQuery(id+"F39.imprint","IMPRINT",FACE,{"disambiguationData":[TD([[makeQuery(id+"F39.imprint","IMPRINT",EDGE,{"derivedFrom":makeQuery(id+"F38.opExtrude","CAP_EDGE",EDGE,{"disambiguationData":[OSD([sQuery(id+"F37.wireOp",EDGE,"E135")])],"isStart":false})}),1.0]])]});
            extrude(context, id + "F40", {"entities" : qUnion([Q0, Q1]), "operationType" : NewBodyOperationType.ADD, "depth" : 25 * mm, "offsetDistance" : 25 * mm});
        }
        {
            var Q0;
            Q0=makeQuery(id+"F40.opExtrude","CAP_EDGE",EDGE,{"disambiguationData":[OSD([sQuery(id+"F39.wireOp",EDGE,"E136.top")])],"isStart":true});
            var Q1;
            Q1=makeQuery(id+"F40.opExtrude","CAP_EDGE",EDGE,{"disambiguationData":[OSD([sQuery(id+"F39.wireOp",EDGE,"E136.bottom")])],"isStart":true});
            chamfer(context, id + "F41", {"entities" : qUnion([Q0, Q1]), "width" : 5 * mm, "tangentPropagation" : true});
        }
        {
            var Q0;
            Q0=makeQuery(id+"F40.opExtrude","CAP_EDGE",EDGE,{"disambiguationData":[OSD([sQuery(id+"F39.wireOp",EDGE,"E136.bottom")])],"isStart":false});
            var Q1;
            Q1=makeQuery(id+"F40.opExtrude","CAP_EDGE",EDGE,{"disambiguationData":[OSD([sQuery(id+"F39.wireOp",EDGE,"E136.top")])],"isStart":false});
            fillet(context, id + "F42", {"entities" : qUnion([Q0, Q1]), "radius" : 3 * mm, "tangentPropagation" : true, "allowEdgeOverflow" : false});
        }
    });
